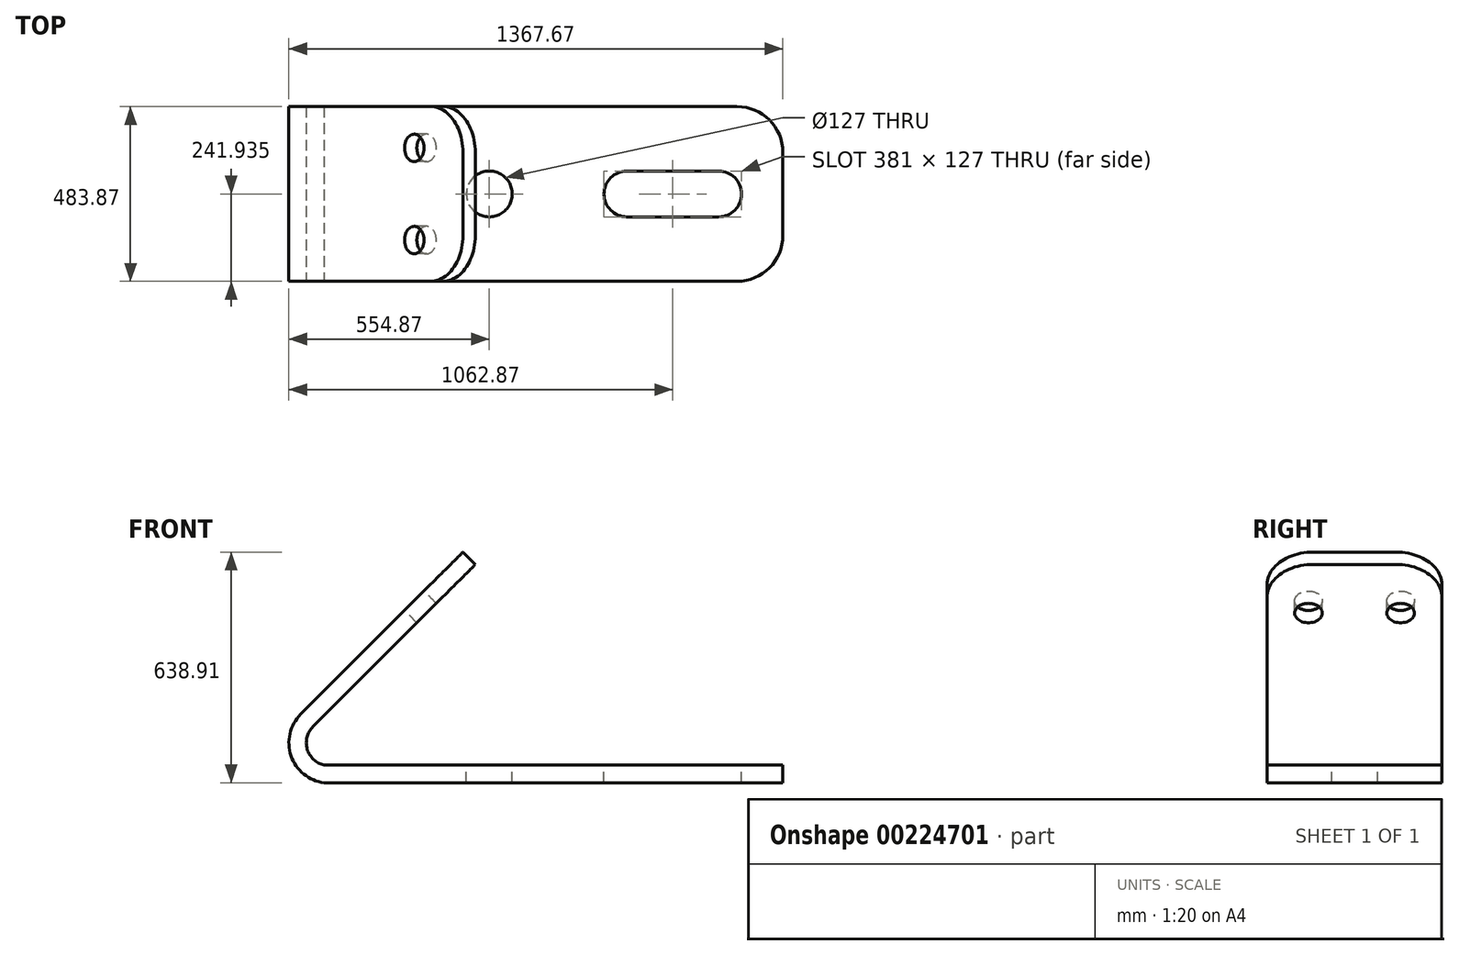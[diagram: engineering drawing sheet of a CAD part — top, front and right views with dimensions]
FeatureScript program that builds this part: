
annotation { "Feature Type Name" : "Feature", "Feature Type Description" : "" }
export const myFeature = defineFeature(function(context is Context, id is Id, definition is map)
    precondition{}
    {
        {
            var Q0;
            Q0=qCreatedBy(makeId("Front.planeOp"),FACE);
            var sketch = newSketch(context, id + "F0", { "sketchPlane" : qUnion([Q0])});
            skLineSegment(sketch, "E0", {"start": v(0, 0) * mm, "end": v(-1270, 0) * mm});
            skArc(sketch, "E1", {"start": v(-1334.94, 189.9) * mm, "mid": v(-1361.66, 74.7) * mm, "end": v(-1270, 0) * mm});
            skLineSegment(sketch, "E2", {"start": v(0, 0) * mm, "end": v(0, 48.95) * mm});
            skLineSegment(sketch, "E3", {"start": v(0, 48.95) * mm, "end": v(-1270, 48.95) * mm});
            skArc(sketch, "E4", {"start": v(-1300.81, 155.77) * mm, "mid": v(-1316.92, 93.27) * mm, "end": v(-1270, 48.95) * mm});
            skLineSegment(sketch, "E5", {"start": v(-1334.94, 189.9) * mm, "end": v(-885.93, 638.9) * mm});
            skLineSegment(sketch, "E6", {"start": v(-885.93, 638.9) * mm, "end": v(-851.8, 604.78) * mm});
            skLineSegment(sketch, "E7", {"start": v(-851.8, 604.78) * mm, "end": v(-1300.81, 155.77) * mm});
            skSolve(sketch);
        }
        {
            var Q0;
            Q0 = qSketchRegion(id + "F0", true);
            extrude(context, id + "F1", {"entities" : qUnion([Q0]), "oppositeDirection" : true, "depth" : 483.87 * mm});
        }
        {
            var Q0;
            Q0=makeQuery(id+"F1.opExtrude","SWEPT_FACE",FACE,{"disambiguationData":[OSD([sQuery(id+"F0.wireOp",EDGE,"E5")])]});
            var sketch = newSketch(context, id + "F2", { "sketchPlane" : qUnion([Q0])});
            skCircle(sketch, "E8", {"center": v(-369.57, -365.17) * mm, "radius": 38.1 * mm});
            skCircle(sketch, "E9", {"center": v(-114.3, -365.17) * mm, "radius": 38.1 * mm});
            skSolve(sketch);
        }
        {
            var Q0;
            Q0 = qSketchRegion(id + "F2", true);
            extrude(context, id + "F3", {"entities" : qUnion([Q0]), "operationType" : NewBodyOperationType.REMOVE, "oppositeDirection" : true, "depth" : 228.6 * mm});
        }
        {
            var Q0;
            Q0=makeQuery(id+"F1.opExtrude","SWEPT_FACE",FACE,{"disambiguationData":[OSD([sQuery(id+"F0.wireOp",EDGE,"E3")])]});
            var sketch = newSketch(context, id + "F4", { "sketchPlane" : qUnion([Q0])});
            skCircle(sketch, "E10", {"center": v(-812.8, 241.93) * mm, "radius": 63.5 * mm});
            skLineSegment(sketch, "E11", {"start": v(0, 241.94) * mm, "end": v(-114.3, 241.94) * mm});
            skLineSegment(sketch, "E12", {"start": v(-114.3, 241.94) * mm, "end": v(-495.3, 241.94) * mm, "construction": true});
            skLineSegment(sketch, "E13.bottom", {"start": v(-114.3, 305.44) * mm, "end": v(-495.3, 305.44) * mm});
            skLineSegment(sketch, "E13.top", {"start": v(-114.3, 178.44) * mm, "end": v(-495.3, 178.44) * mm});
            skLineSegment(sketch, "E13.left", {"start": v(-114.3, 305.44) * mm, "end": v(-114.3, 178.44) * mm});
            skLineSegment(sketch, "E13.right", {"start": v(-495.3, 305.44) * mm, "end": v(-495.3, 178.44) * mm});
            skPoint(sketch, "E13.middle", {"position": v(-304.8, 241.94) * mm});
            skLineSegment(sketch, "E14", {"start": v(-495.3, 241.94) * mm, "end": v(-431.8, 241.94) * mm});
            skLineSegment(sketch, "E15", {"start": v(-114.3, 241.94) * mm, "end": v(-177.8, 241.94) * mm});
            skCircle(sketch, "E16", {"center": v(-431.8, 241.94) * mm, "radius": 63.5 * mm});
            skCircle(sketch, "E17", {"center": v(-177.8, 241.94) * mm, "radius": 63.5 * mm});
            skSolve(sketch);
        }
        {
            var Q0;
            {var subQ0=sQuery(id+"F4.wireOp",EDGE,"E16");var subQ1=makeQuery(id+"F4.imprint","INTERSECT",VERTEX,{"derivedFrom":[sQuery(id+"F4.wireOp",EDGE,"E13.right"),subQ0]});Q0=makeQuery(id+"F4.imprint","IMPRINT",FACE,{"disambiguationData":[TD([[makeQuery(id+"F4.imprint","IMPRINT",EDGE,{"disambiguationData":[TD([[subQ1,1.0]])],"derivedFrom":subQ0}),1.0]])]});}
            var Q1;
            {var subQ0=sQuery(id+"F4.wireOp",EDGE,"E17");var subQ1=sQuery(id+"F4.wireOp",EDGE,"E13.bottom");var subQ2=makeQuery(id+"F4.imprint","INTERSECT",VERTEX,{"derivedFrom":[subQ1,subQ0]});Q1=makeQuery(id+"F4.imprint","IMPRINT",FACE,{"disambiguationData":[TD([[makeQuery(id+"F4.imprint","IMPRINT",EDGE,{"disambiguationData":[TD([[subQ2,-1.0]])],"derivedFrom":subQ1}),1.0]])]});}
            var Q2;
            {var subQ0=sQuery(id+"F4.wireOp",EDGE,"E17");var subQ1=makeQuery(id+"F4.imprint","INTERSECT",VERTEX,{"derivedFrom":[sQuery(id+"F4.wireOp",EDGE,"E13.left"),subQ0]});Q2=makeQuery(id+"F4.imprint","IMPRINT",FACE,{"disambiguationData":[TD([[makeQuery(id+"F4.imprint","IMPRINT",EDGE,{"disambiguationData":[TD([[subQ1,-1.0]])],"derivedFrom":subQ0}),1.0]])]});}
            var Q3;
            Q3=makeQuery(id+"F4.imprint","IMPRINT",FACE,{"disambiguationData":[TD([[makeQuery(id+"F4.imprint","IMPRINT",EDGE,{"derivedFrom":sQuery(id+"F4.wireOp",EDGE,"E10")}),1.0]])]});
            extrude(context, id + "F5", {"entities" : qUnion([Q0, Q1, Q2, Q3]), "operationType" : NewBodyOperationType.REMOVE, "oppositeDirection" : true, "depth" : 421.64 * mm});
        }
        {
            var Q0;
            Q0=makeQuery(id+"F1.opExtrude","CAP_EDGE",EDGE,{"disambiguationData":[OSD([sQuery(id+"F0.wireOp",EDGE,"E6")])],"isStart":true});
            var Q1;
            Q1=makeQuery(id+"F1.opExtrude","CAP_EDGE",EDGE,{"disambiguationData":[OSD([sQuery(id+"F0.wireOp",EDGE,"E6")])],"isStart":false});
            var Q2;
            Q2=makeQuery(id+"F1.opExtrude","CAP_EDGE",EDGE,{"disambiguationData":[OSD([sQuery(id+"F0.wireOp",EDGE,"E2")])],"isStart":true});
            var Q3;
            Q3=makeQuery(id+"F1.opExtrude","CAP_EDGE",EDGE,{"disambiguationData":[OSD([sQuery(id+"F0.wireOp",EDGE,"E2")])],"isStart":false});
            fillet(context, id + "F6", {"entities" : qUnion([Q0, Q1, Q2, Q3]), "radius" : 127 * mm, "tangentPropagation" : true, "allowEdgeOverflow" : false});
        }
    });
